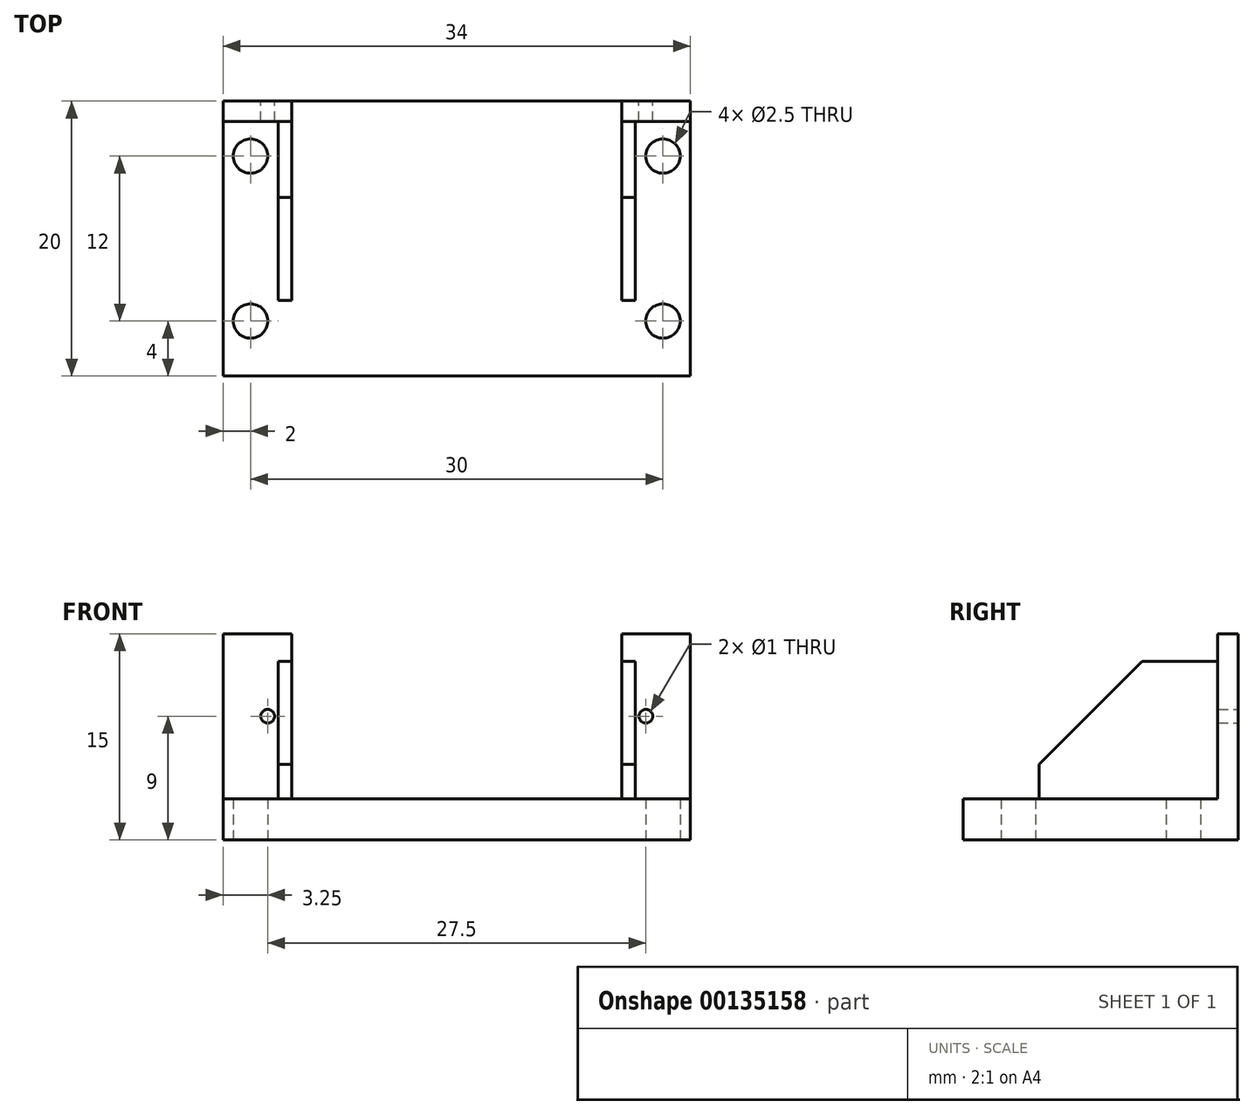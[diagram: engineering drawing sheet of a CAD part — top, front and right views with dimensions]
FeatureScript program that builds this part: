
annotation { "Feature Type Name" : "Feature", "Feature Type Description" : "" }
export const myFeature = defineFeature(function(context is Context, id is Id, definition is map)
    precondition{}
    {
        {
            var Q0;
            Q0=qCreatedBy(makeId("Top.planeOp"),FACE);
            var sketch = newSketch(context, id + "F0", { "sketchPlane" : qUnion([Q0])});
            skPoint(sketch, "E0.middle", {"position": v(0, 0) * mm});
            skLineSegment(sketch, "E1.bottom", {"start": v(17, 10) * mm, "end": v(-17, 10) * mm});
            skLineSegment(sketch, "E1.top", {"start": v(17, -10) * mm, "end": v(-17, -10) * mm});
            skLineSegment(sketch, "E1.left", {"start": v(17, 10) * mm, "end": v(17, -10) * mm});
            skLineSegment(sketch, "E1.right", {"start": v(-17, 10) * mm, "end": v(-17, -10) * mm});
            skLineSegment(sketch, "E2.bottom", {"start": v(15, -6) * mm, "end": v(-15, -6) * mm, "construction": true});
            skLineSegment(sketch, "E2.top", {"start": v(15, 6) * mm, "end": v(-15, 6) * mm, "construction": true});
            skLineSegment(sketch, "E2.left", {"start": v(15, -6) * mm, "end": v(15, 6) * mm, "construction": true});
            skLineSegment(sketch, "E2.right", {"start": v(-15, -6) * mm, "end": v(-15, 6) * mm, "construction": true});
            skCircle(sketch, "E3", {"center": v(-15, 6) * mm, "radius": 1.25 * mm});
            skCircle(sketch, "E4", {"center": v(15, 6) * mm, "radius": 1.25 * mm});
            skCircle(sketch, "E5", {"center": v(15, -6) * mm, "radius": 1.25 * mm});
            skCircle(sketch, "E6", {"center": v(-15, -6) * mm, "radius": 1.25 * mm});
            skSolve(sketch);
        }
        {
            var Q0;
            Q0=makeQuery(id+"F0.imprint","IMPRINT",FACE,{"disambiguationData":[TD([[makeQuery(id+"F0.imprint","IMPRINT",EDGE,{"derivedFrom":sQuery(id+"F0.wireOp",EDGE,"E1.bottom")}),1.0]])]});
            extrude(context, id + "F1", {"entities" : qUnion([Q0]), "depth" : 3 * mm});
        }
        {
            var Q0;
            Q0=makeQuery(id+"F1.opExtrude","CAP_FACE",FACE,{"disambiguationData":[OSD([sQuery(id+"F0.wireOp",EDGE,"E1.bottom"),sQuery(id+"F0.wireOp",EDGE,"E1.top"),sQuery(id+"F0.wireOp",EDGE,"E1.left"),sQuery(id+"F0.wireOp",EDGE,"E1.right"),sQuery(id+"F0.wireOp",EDGE,"vzK1fUSa-lQ93-gUsW-PDJR-nfCJ2R12phpp"),sQuery(id+"F0.wireOp",EDGE,"02D62mhn-a1J2-C6ph-PN2Y-qU2xGVv3P8Oz"),sQuery(id+"F0.wireOp",EDGE,"pFrEjN4t-njIc-1peO-OumG-HhqZBXLBqHxK"),sQuery(id+"F0.wireOp",EDGE,"S4G6YkLf-4ES2-Bgjt-2d77-uvgpIk0Qyx0L")])],"isStart":false});
            var sketch = newSketch(context, id + "F2", { "sketchPlane" : qUnion([Q0])});
            skLineSegment(sketch, "E7.bottom", {"start": v(-17, 10) * mm, "end": v(-12, 10) * mm});
            skLineSegment(sketch, "E7.top", {"start": v(-17, 8.5) * mm, "end": v(-12, 8.5) * mm});
            skLineSegment(sketch, "E7.left", {"start": v(-17, 10) * mm, "end": v(-17, 8.5) * mm});
            skLineSegment(sketch, "E7.right", {"start": v(-12, 10) * mm, "end": v(-12, 8.5) * mm});
            skLineSegment(sketch, "E8.bottom", {"start": v(17, 10) * mm, "end": v(12, 10) * mm});
            skLineSegment(sketch, "E8.top", {"start": v(17, 8.5) * mm, "end": v(12, 8.5) * mm});
            skLineSegment(sketch, "E8.left", {"start": v(17, 10) * mm, "end": v(17, 8.5) * mm});
            skLineSegment(sketch, "E8.right", {"start": v(12, 10) * mm, "end": v(12, 8.5) * mm});
            skPoint(sketch, "E9", {"position": v(-12, 8.5) * mm});
            skPoint(sketch, "E10", {"position": v(12, 8.5) * mm});
            skSolve(sketch);
        }
        {
            var Q0;
            Q0=makeQuery(id+"F2.imprint","IMPRINT",FACE,{"disambiguationData":[TD([[makeQuery(id+"F2.imprint","IMPRINT",EDGE,{"derivedFrom":sQuery(id+"F2.wireOp",EDGE,"E7.bottom")}),1.0]])]});
            var Q1;
            Q1=makeQuery(id+"F2.imprint","IMPRINT",FACE,{"disambiguationData":[TD([[makeQuery(id+"F2.imprint","IMPRINT",EDGE,{"derivedFrom":sQuery(id+"F2.wireOp",EDGE,"E8.bottom")}),1.0]])]});
            var Q2;
            Q2=makeQuery(id+"F2.imprint","IMPRINT",FACE,{"disambiguationData":[TD([[makeQuery(id+"F2.imprint","IMPRINT",EDGE,{"derivedFrom":sQuery(id+"F2.wireOp",EDGE,"qa5opf6L-vfva-f9ps-wdat-dUW7fVkKqp9T.bottom")}),-1.0]])]});
            var Q3;
            Q3=makeQuery(id+"F2.imprint","IMPRINT",FACE,{"disambiguationData":[TD([[makeQuery(id+"F2.imprint","IMPRINT",EDGE,{"derivedFrom":sQuery(id+"F2.wireOp",EDGE,"lnxaC5Hq-gqwb-D7rE-EtE1-ObI2EhhsYE1f.bottom")}),-1.0]])]});
            extrude(context, id + "F3", {"entities" : qUnion([Q0, Q1, Q2, Q3]), "operationType" : NewBodyOperationType.ADD, "depth" : 12 * mm});
        }
        {
            var Q0;
            Q0=makeQuery(id+"F1.opExtrude","CAP_FACE",FACE,{"disambiguationData":[OSD([sQuery(id+"F0.wireOp",EDGE,"E1.bottom"),sQuery(id+"F0.wireOp",EDGE,"E1.top"),sQuery(id+"F0.wireOp",EDGE,"E1.left"),sQuery(id+"F0.wireOp",EDGE,"E1.right"),sQuery(id+"F0.wireOp",EDGE,"vzK1fUSa-lQ93-gUsW-PDJR-nfCJ2R12phpp"),sQuery(id+"F0.wireOp",EDGE,"02D62mhn-a1J2-C6ph-PN2Y-qU2xGVv3P8Oz"),sQuery(id+"F0.wireOp",EDGE,"pFrEjN4t-njIc-1peO-OumG-HhqZBXLBqHxK"),sQuery(id+"F0.wireOp",EDGE,"S4G6YkLf-4ES2-Bgjt-2d77-uvgpIk0Qyx0L")])],"isStart":false});
            var sketch = newSketch(context, id + "F4", { "sketchPlane" : qUnion([Q0])});
            skLineSegment(sketch, "E11.bottom", {"start": v(-12, 8.5) * mm, "end": v(-13, 8.5) * mm});
            skLineSegment(sketch, "E11.top", {"start": v(-12, -4.5) * mm, "end": v(-13, -4.5) * mm});
            skLineSegment(sketch, "E11.left", {"start": v(-12, 8.5) * mm, "end": v(-12, -4.5) * mm});
            skLineSegment(sketch, "E11.right", {"start": v(-13, 8.5) * mm, "end": v(-13, -4.5) * mm});
            skLineSegment(sketch, "E12.bottom", {"start": v(12, 8.5) * mm, "end": v(13, 8.5) * mm});
            skLineSegment(sketch, "E12.top", {"start": v(12, -4.5) * mm, "end": v(13, -4.5) * mm});
            skLineSegment(sketch, "E12.left", {"start": v(12, 8.5) * mm, "end": v(12, -4.5) * mm});
            skLineSegment(sketch, "E12.right", {"start": v(13, 8.5) * mm, "end": v(13, -4.5) * mm});
            skSolve(sketch);
        }
        {
            var Q0;
            Q0=qSketchRegion(id+"F4",true);
            extrude(context, id + "F5", {"entities" : qUnion([Q0]), "operationType" : NewBodyOperationType.ADD, "depth" : 10 * mm});
        }
        {
            var Q0;
            Q0=makeQuery(id+"F5.opExtrude","CAP_EDGE",EDGE,{"disambiguationData":[OSD([sQuery(id+"F4.wireOp",EDGE,"E11.top")])],"isStart":false});
            var Q1;
            Q1=makeQuery(id+"F5.opExtrude","CAP_EDGE",EDGE,{"disambiguationData":[OSD([sQuery(id+"F4.wireOp",EDGE,"E12.top")])],"isStart":false});
            chamfer(context, id + "F6", {"entities" : qUnion([Q0, Q1]), "width" : 7.5 * mm, "tangentPropagation" : true});
        }
        {
            var Q0;
            Q0=makeQuery(id+"F3.boolean.opBoolean","MERGE",FACE,{"derivedFrom":[makeQuery(id+"F1.opExtrude","SWEPT_FACE",FACE,{"disambiguationData":[OSD([sQuery(id+"F0.wireOp",EDGE,"E1.bottom")])]}),makeQuery(id+"F3.opExtrude","SWEPT_FACE",FACE,{"disambiguationData":[OSD([sQuery(id+"F2.wireOp",EDGE,"E7.bottom")])]}),makeQuery(id+"F3.opExtrude","SWEPT_FACE",FACE,{"disambiguationData":[OSD([sQuery(id+"F2.wireOp",EDGE,"E8.bottom")])]})]});
            var sketch = newSketch(context, id + "F7", { "sketchPlane" : qUnion([Q0])});
            skLineSegment(sketch, "E13.bottom", {"start": v(-13.75, 9) * mm, "end": v(13.75, 9) * mm, "construction": true});
            skLineSegment(sketch, "E13.top", {"start": v(-13.75, -9) * mm, "end": v(13.75, -9) * mm, "construction": true});
            skLineSegment(sketch, "E13.left", {"start": v(-13.75, 9) * mm, "end": v(-13.75, -9) * mm, "construction": true});
            skLineSegment(sketch, "E13.right", {"start": v(13.75, 9) * mm, "end": v(13.75, -9) * mm, "construction": true});
            skPoint(sketch, "E13.middle", {"position": v(0, 0) * mm});
            skPoint(sketch, "E14", {"position": v(13.75, 9) * mm});
            skPoint(sketch, "E15", {"position": v(-13.75, 9) * mm});
            skSolve(sketch);
        }
        {
            var Q0;
            Q0=sQuery(id+"F7.wireOp",VERTEX,"E14");
            var Q1;
            Q1=sQuery(id+"F7.wireOp",VERTEX,"E15");
            var Q2;
            Q2=makeQuery(id+"F1.opExtrude","SWEPT_BODY",BODY,{"disambiguationData":[OSD([sQuery(id+"F0.wireOp",EDGE,"E1.bottom"),sQuery(id+"F0.wireOp",EDGE,"E1.top"),sQuery(id+"F0.wireOp",EDGE,"E1.left"),sQuery(id+"F0.wireOp",EDGE,"E1.right"),sQuery(id+"F0.wireOp",EDGE,"vzK1fUSa-lQ93-gUsW-PDJR-nfCJ2R12phpp"),sQuery(id+"F0.wireOp",EDGE,"02D62mhn-a1J2-C6ph-PN2Y-qU2xGVv3P8Oz"),sQuery(id+"F0.wireOp",EDGE,"pFrEjN4t-njIc-1peO-OumG-HhqZBXLBqHxK"),sQuery(id+"F0.wireOp",EDGE,"S4G6YkLf-4ES2-Bgjt-2d77-uvgpIk0Qyx0L")])]});
            hole(context, id + "F8", {"style" : HoleStyle.SIMPLE, "endStyle" : HoleEndStyle.THROUGH, "holeDiameter" : 1 * mm, "locations" : qUnion([Q0, Q1]), "scope" : qUnion([Q2]), "isTappedThrough" : true});
        }
    });
